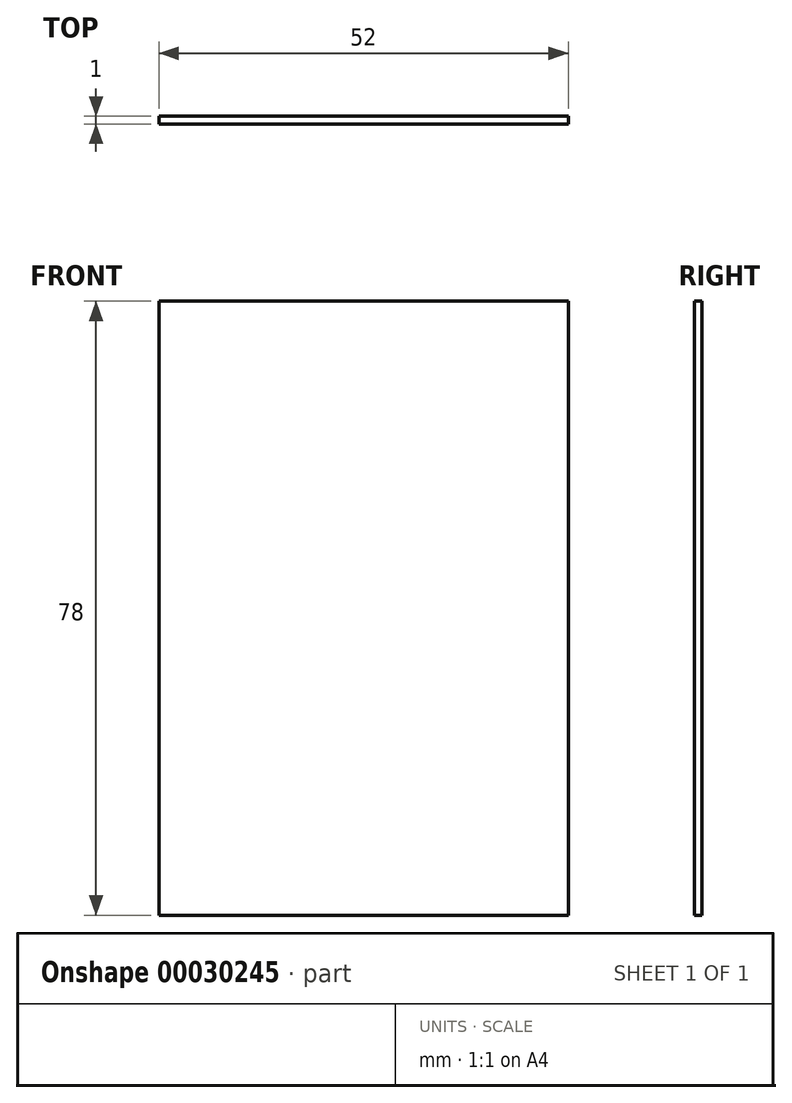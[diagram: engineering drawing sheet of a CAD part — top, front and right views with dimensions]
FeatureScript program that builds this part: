
annotation { "Feature Type Name" : "Feature", "Feature Type Description" : "" }
export const myFeature = defineFeature(function(context is Context, id is Id, definition is map)
    precondition{}
    {
        {
            var Q0;
            Q0=qCreatedBy(makeId("Front.planeOp"),FACE);
            var sketch = newSketch(context, id + "F0", { "sketchPlane" : qUnion([Q0])});
            skLineSegment(sketch, "E0.bottom", {"start": v(-26, 39) * mm, "end": v(26, 39) * mm});
            skLineSegment(sketch, "E0.top", {"start": v(-26, -39) * mm, "end": v(26, -39) * mm});
            skLineSegment(sketch, "E0.left", {"start": v(-26, 39) * mm, "end": v(-26, -39) * mm});
            skLineSegment(sketch, "E0.right", {"start": v(26, 39) * mm, "end": v(26, -39) * mm});
            skPoint(sketch, "E0.middle", {"position": v(0, 0) * mm});
            skSolve(sketch);
        }
        {
            var Q0;
            Q0=makeQuery(id+"F0.imprint","IMPRINT",FACE,{"disambiguationData":[TD([[makeQuery(id+"F0.imprint","IMPRINT",EDGE,{"derivedFrom":sQuery(id+"F0.wireOp",EDGE,"E0.bottom")}),-1.0]])]});
            extrude(context, id + "F1", {"entities" : qUnion([Q0]), "depth" : 1 * mm});
        }
    });
